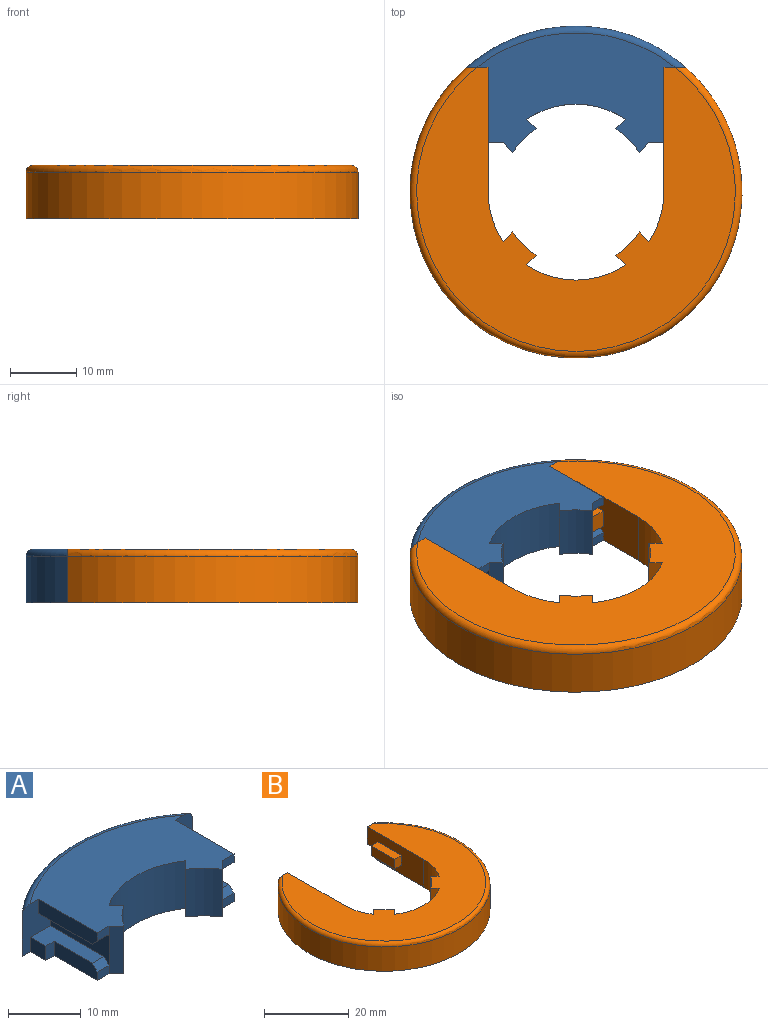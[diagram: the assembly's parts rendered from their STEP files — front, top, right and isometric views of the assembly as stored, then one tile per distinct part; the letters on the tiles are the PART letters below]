
ASSEMBLY  parts=2 mates=1
PART A: 35 faces, bbox 35.7x21.1x8 mm
  f0: plane 8.37x2.4mm, normal (1,0,0), area 19.6mm2, adj f3,f8,f22,f29,f33
  f1: plane 8.37x2.4mm, normal (-1,0,0), area 19.6mm2, adj f2,f8,f25,f26,f31
  f2: plane 2.28x1.4mm, normal (0,-1,0), area 3.2mm2, adj f1,f8,f10,f26
  f3: plane 2.28x1.4mm, normal (0,-1,0), area 3.2mm2, adj f0,f8,f16,f29
  f4: plane 11.37x2.4mm, normal (1,0,0), area 26.8mm2, adj f7,f17,f19,f21,f28
  f5: plane 11.37x2.4mm, normal (-1,0,0), area 26.8mm2, adj f7,f9,f18,f24,f27
  f6: cylinder r=25mm len=32.96mm, axis (0,0,-1), area 251.9mm2, adj f8,f18,f19,f30
  f7: plane 29.84x18.01mm, normal (0,0,1), area 337.6mm2, adj f4,f5,f9,f10,f11,f12,f13,f14
  f8: plane 32.96x19.01mm, normal (0,0,-1), area 381.4mm2, adj f0,f1,f2,f3,f6,f10,f11,f12
  f9: plane 2.28x1.4mm, normal (0,-1,0), area 3.2mm2, adj f5,f7,f10,f27
  f10: plane 8x1.45mm, normal (-0.71,-0.71,0), area 16.3mm2, adj f2,f7,f8,f9,f11,f23
  f11: cylinder r=11.25mm len=8mm, axis (0,0,-1), area 40.3mm2, adj f7,f8,f10,f12
  f12: plane 8x1.45mm, normal (0.71,0.71,0), area 16.3mm2, adj f7,f8,f11,f13
  f13: cylinder r=13.25mm len=14.87mm, axis (0,0,-1), area 126.3mm2, adj f7,f8,f12,f14
  f14: plane 8x1.45mm, normal (-0.71,0.71,0), area 16.3mm2, adj f7,f8,f13,f15
  f15: cylinder r=11.25mm len=8mm, axis (0,0,-1), area 40.3mm2, adj f7,f8,f14,f16
  f16: plane 8x1.45mm, normal (0.71,-0.71,0), area 16.3mm2, adj f3,f7,f8,f15,f17,f20
  f17: plane 2.28x1.4mm, normal (0,-1,0), area 3.2mm2, adj f4,f7,f16,f28
  f18: plane 8x5.51mm, normal (0,-1,0), area 28.9mm2, adj f5,f6,f7,f8,f23,f24,f25,f30
  f19: plane 8x5.51mm, normal (0,-1,0), area 28.9mm2, adj f4,f6,f7,f8,f20,f21,f22,f30
  f20: plane 11.37x5.2mm, normal (1,0,0), area 37.4mm2, adj f16,f19,f21,f22,f28,f29
  f21: plane 10.37x2.28mm, normal (0,0,-1), area 23.7mm2, adj f4,f19,f20,f28
  f22: plane 10.37x3.9mm, normal (0,0,1), area 28.5mm2, adj f0,f19,f20,f29,f33,f34
  f23: plane 11.37x5.2mm, normal (-1,0,0), area 37.4mm2, adj f10,f18,f24,f25,f26,f27
  f24: plane 10.37x2.28mm, normal (0,0,-1), area 23.7mm2, adj f5,f18,f23,f27
  f25: plane 10.37x3.9mm, normal (0,0,1), area 28.5mm2, adj f1,f18,f23,f26,f31,f32
  f26: plane 2.28x1mm, normal (0,-0.71,0.71), area 3.2mm2, adj f1,f2,f23,f25
  f27: plane 2.28x1mm, normal (0,-0.71,-0.71), area 3.2mm2, adj f5,f9,f23,f24
  f28: plane 2.28x1mm, normal (0,-0.71,-0.71), area 3.2mm2, adj f4,f17,f20,f21
  f29: plane 2.28x1mm, normal (0,-0.71,0.71), area 3.2mm2, adj f0,f3,f20,f22
  f30: torus R=24mm, axis (0,0,1), area 54.4mm2, adj f6,f7,f18,f19
  f31: plane 2.4x1.61mm, normal (0,-1,0), area 3.9mm2, adj f1,f8,f25,f32
  f32: plane 3x2.4mm, normal (-1,0,0), area 7.2mm2, adj f8,f18,f25,f31
  f33: plane 2.4x1.61mm, normal (0,-1,0), area 3.9mm2, adj f0,f8,f22,f34
  f34: plane 3x2.4mm, normal (1,0,0), area 7.2mm2, adj f8,f19,f22,f33
PART B: 39 faces, bbox 54.1x48.3x8 mm
  f0: plane 7.77x2.8mm, normal (1,0,0), area 21.7mm2, adj f26,f27,f28,f36
  f1: plane 7.77x2.8mm, normal (-1,0,0), area 21.7mm2, adj f2,f3,f29,f33
  f2: plane 7.77x2.28mm, normal (0,0,1), area 17.7mm2, adj f1,f4,f29,f32
  f3: plane 7.77x2.28mm, normal (0,0,-1), area 17.7mm2, adj f1,f4,f29,f34
  f4: plane 18.8x8mm, normal (-1,0,0), area 117.9mm2, adj f2,f3,f6,f9,f10,f19,f20,f22
  f5: plane 18.8x8mm, normal (1,0,0), area 117.9mm2, adj f6,f7,f18,f19,f24,f25,f26,f27
  f6: plane 50x43.8mm, normal (0,0,-1), area 1060mm2, adj f4,f5,f7,f8,f9,f10,f11,f12
  f7: plane 8x3.23mm, normal (0,1,0), area 20.7mm2, adj f5,f6,f8,f19,f23,f25,f38
  f8: cylinder r=25mm len=50mm, axis (0,0,-1), area 847.7mm2, adj f6,f7,f9,f38
  f9: plane 8x3.23mm, normal (0,1,0), area 20.7mm2, adj f4,f6,f8,f19,f21,f22,f38
  f10: cylinder r=13.25mm len=8mm, axis (0,0,-1), area 63.1mm2, adj f4,f6,f11,f19
  f11: plane 8x1.45mm, normal (0.71,0.71,0), area 16.3mm2, adj f6,f10,f12,f19
  f12: cylinder r=11.25mm len=8mm, axis (0,0,-1), area 40.3mm2, adj f6,f11,f13,f19
  f13: plane 8x1.45mm, normal (-0.71,-0.71,0), area 16.3mm2, adj f6,f12,f14,f19
  f14: cylinder r=13.25mm len=14.87mm, axis (0,0,-1), area 126.3mm2, adj f6,f13,f15,f19
  f15: plane 8x1.45mm, normal (0.71,-0.71,0), area 16.3mm2, adj f6,f14,f16,f19
  f16: cylinder r=11.25mm len=8mm, axis (0,0,-1), area 40.3mm2, adj f6,f15,f17,f19
  f17: plane 8x1.45mm, normal (-0.71,0.71,0), area 16.3mm2, adj f6,f16,f18,f19
  f18: cylinder r=13.25mm len=8mm, axis (0,0,-1), area 63.1mm2, adj f5,f6,f17,f19
  f19: plane 48x42.8mm, normal (0,0,1), area 949.8mm2, adj f4,f5,f7,f9,f10,f11,f12,f13
  f20: plane 3x1.61mm, normal (0,1,0), area 4.8mm2, adj f4,f6,f21,f22
  f21: plane 3x3mm, normal (-1,0,0), area 9mm2, adj f6,f9,f20,f22
  f22: plane 3x1.61mm, normal (0,0,-1), area 4.8mm2, adj f4,f9,f20,f21
  f23: plane 3x3mm, normal (1,0,0), area 9mm2, adj f6,f7,f24,f25
  f24: plane 3x1.61mm, normal (0,1,0), area 4.8mm2, adj f5,f6,f23,f25
  f25: plane 3x1.61mm, normal (0,0,-1), area 4.8mm2, adj f5,f7,f23,f24
  f26: plane 2.8x2.28mm, normal (0,-1,0), area 6.4mm2, adj f0,f5,f27,f28
  f27: plane 7.77x2.28mm, normal (0,0,1), area 17.7mm2, adj f0,f5,f26,f35
  f28: plane 7.77x2.28mm, normal (0,0,-1), area 17.7mm2, adj f0,f5,f26,f37
  f29: plane 2.8x2.28mm, normal (0,-1,0), area 6.4mm2, adj f1,f2,f3,f4
  f30: plane 1.28x0.8mm, normal (0,1,0), area 1mm2, adj f4,f32,f33,f34
  f31: plane 1.28x0.8mm, normal (0,1,0), area 1mm2, adj f5,f35,f36,f37
  f32: plane 2.28x1mm, normal (0,0.71,0.71), area 2.5mm2, adj f2,f4,f30,f33
  f33: plane 2.8x1mm, normal (-0.71,0.71,0), area 2.5mm2, adj f1,f30,f32,f34
  f34: plane 2.28x1mm, normal (0,0.71,-0.71), area 2.5mm2, adj f3,f4,f30,f33
  f35: plane 2.28x1mm, normal (0,0.71,0.71), area 2.5mm2, adj f5,f27,f31,f36
  f36: plane 2.8x1mm, normal (0.71,0.71,0), area 2.5mm2, adj f0,f31,f35,f37
  f37: plane 2.28x1mm, normal (0,0.71,-0.71), area 2.5mm2, adj f5,f28,f31,f36
  f38: torus R=24mm, axis (0,0,1), area 188.8mm2, adj f7,f8,f9,f19
PLACE A at identity
PLACE B at identity
MATE slider A.f33 <-> B.f20  axis (0,1,0) through (13.25,15.8,0)mm
